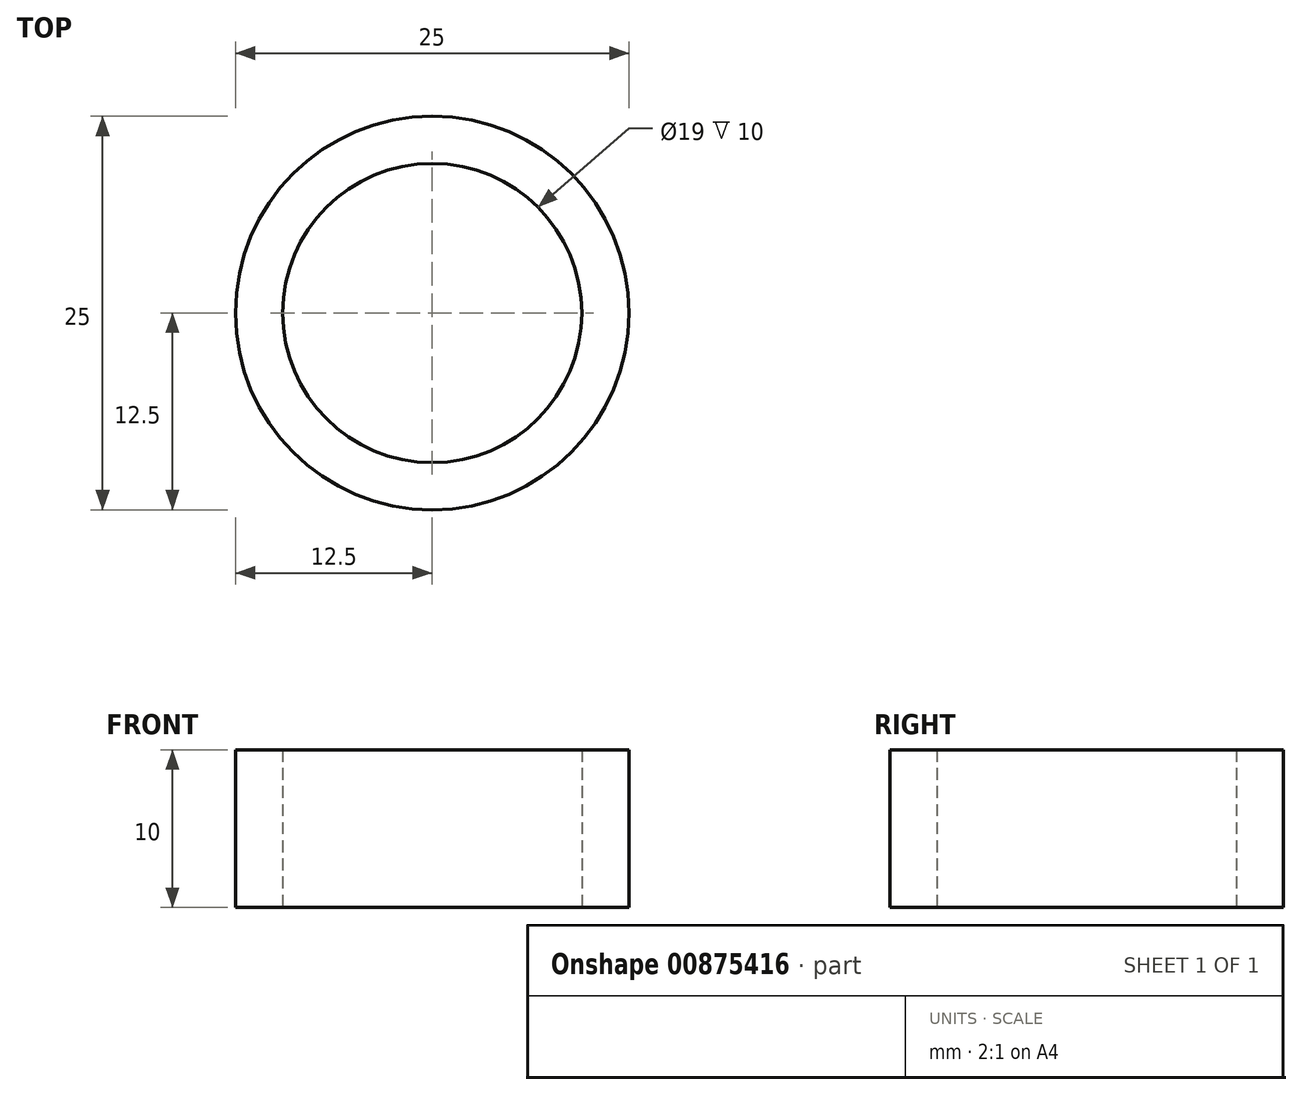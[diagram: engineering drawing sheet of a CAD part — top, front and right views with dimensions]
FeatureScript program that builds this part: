
annotation { "Feature Type Name" : "Feature", "Feature Type Description" : "" }
export const myFeature = defineFeature(function(context is Context, id is Id, definition is map)
    precondition{}
    {
        {
            var Q0;
            Q0=qCreatedBy(makeId("Top.planeOp"),FACE);
            var sketch = newSketch(context, id + "F0", { "sketchPlane" : qUnion([Q0])});
            skCircle(sketch, "E0", {"center": v(0, 0) * mm, "radius": 9.5 * mm});
            skCircle(sketch, "E1", {"center": v(0, 0) * mm, "radius": 12.5 * mm});
            skSolve(sketch);
        }
        {
            var Q0;
            Q0 = qSketchRegion(id + "F0", true);
            extrude(context, id + "F1", {"entities" : qUnion([Q0]), "depth" : 10 * mm, "offsetDistance" : 25 * mm});
        }
        {
            var Q0;
            Q0=makeQuery(id+"F1.opExtrude","CAP_FACE",FACE,{"disambiguationData":[OSD([sQuery(id+"F0.wireOp",EDGE,"E0"),sQuery(id+"F0.wireOp",EDGE,"E1")])],"isStart":false});
            var sketch = newSketch(context, id + "F2", { "sketchPlane" : qUnion([Q0])});
            skLineSegment(sketch, "E2.bottom", {"start": v(23.3, -1.68) * mm, "end": v(13.53, -1.68) * mm});
            skLineSegment(sketch, "E2.top", {"start": v(23.3, 1.68) * mm, "end": v(13.53, 1.68) * mm});
            skLineSegment(sketch, "E2.left", {"start": v(23.3, -1.68) * mm, "end": v(23.3, 1.68) * mm});
            skLineSegment(sketch, "E2.right", {"start": v(13.53, -1.68) * mm, "end": v(13.53, 1.68) * mm});
            skPoint(sketch, "E2.middle", {"position": v(18.42, 0) * mm});
            skCircle(sketch, "E3", {"center": v(-16.07, 0) * mm, "radius": 1 * mm});
            skCircle(sketch, "E4.0", {"center": v(-16.07, 0) * mm, "radius": 3 * mm});
            skLineSegment(sketch, "E5", {"start": v(-14.08, 2.24) * mm, "end": v(-11.56, 4.76) * mm});
            skSolve(sketch);
        }
        {
            var Q0;
            Q0 = qSketchRegion(id + "F2", true);
            extrude(context, id + "F3", {"entities" : qUnion([Q0]), "operationType" : NewBodyOperationType.REMOVE, "endBound" : BoundingType.THROUGH_ALL, "oppositeDirection" : true, "depth" : 25 * mm, "offsetDistance" : 25 * mm});
        }
    });
